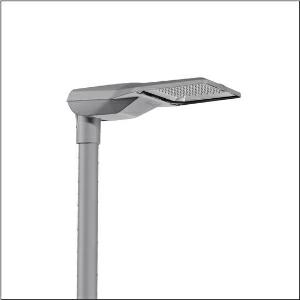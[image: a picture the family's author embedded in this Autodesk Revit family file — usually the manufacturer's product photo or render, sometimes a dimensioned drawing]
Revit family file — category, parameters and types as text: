
# Revit family: streetlight_sl_21_iq_midi___st0_5a_5xe3b41g08mb_6195
name_source: partatom
category: Lighting Fixtures
units: mm (PartAtom-declared; Revit-internal decimal feet)

## family parameters
Cut with Voids When Loaded = No
Host = Face
Light Source = No
Part Type = Normal
Room Calculation Point = No
Round Connector Dimension = Use Diameter
Shared = No

## types (1)
- --- (1 x LED, 20360 lm, 146.7 W, 4000K)
    Apparent Load = 147 VA
    CIE Flux Codes = 41 75 97 100 100
    Color Rendering = 70
    Color Temperature = 4000K
    Default Elevation = 1800 mm
    Description = Streetlight SL 21 iQ midi, mast luminaire, primary light control with lens, of PMMA, primary optical cover: cover, of toughened safety glass, transparent, light distribution: ST0.5a, light emission: direct distribution, primary light characteristic: asymmetric, installation type: post-top, side-entry, LED, High Power LED, rated luminous flux: 20.360lm, luminous efficacy: 139lm/W, light colour: 740, colour temperature: 4000K, control: Street-Remote, Auto-Match, Temp-Guard, Lumen-Switch, Night-Set, Smart-Wire, Light-Fading, Desk-Remote (wireless, voltage-free reading and setting of iQ features in the workshop via application-optimized NFC function/RFID function), optimised constant luminous flux control (CLO 2.0), presetting dimming linear, mains connection: 230..240V, AC, 50/60Hz, start of lifetime: 147W, end of service life: 161W, reduction: 62W, luminaire housing, of diecast aluminium, powder-coated, Siteco® metallic grey (DB 702S), corrosivity category C5 mid according to DIN EN ISO 12944, please order mast flange separately, inclination adjustable: 0°, 5°, 10°, 15°, sealing non-destructively replaceable, multi-level sealing system, length: 644mm, width: 335mm, height: 110mm, mast flange for spigot size: 42mm (side-entry): 5XC10008XM4, 60/48mm (side-entry/post-top): 5XC10108XM2, 76/60mm (side-entry/post-top): 5XC10108XM1, protection rating (complete): IP66, insulation class (complete): insulation class II (safety insulation), certification: CE, ENEC, ENEC+, VDE, impact resistance: IK09, permissible operating ambient temperature for outdoor applications: -40..+50°C, standard-compliant lighting for roads and squares, packaging unit: 1 piece

Light Distribution: ST0.5a
    Height = 111 mm
    Lamp = 1 x LED
    Lamp Light Flux = 20360 lm
    Lamp Power = 146.7 W
    Lamp count = 1
    Length = 644 mm
    Luminous efficacy = 139 lm/W
    Manufacturer = Siteco
    ModVariant = No
    Model = 5XE3B41G08MB
    Number of Poles = 1
    OnlyDefault = Yes
    Power Factor = 1
    Product Name = Streetlight SL 21 iQ midi | ST0.5a
    Product group = mast luminaire | pylon top
    ProductGroupID = 6100
    Protection Class = Protection class II
    Protection Degree = IP 66
    RLX_Detail_Level = 1
    RLX_Emergency_Light_Flux = 0 lm
    RLX_Emergency_Type = 0
    RLX_Emergency_Type_DB = No
    RlxData = <blob elided: 101621 chars, md5=bc9abe9a>
    Socket = socket
    Standby Power = 0 W
    System Light Flux = 20360 lm
    System Power = 147 W
    Type Comments = factory setting: luminous flux: 100 % | dim-lin: 254 | 753 mA
    Type Image = l_1004298.jpg
    URL = http://relux.com
    VarID = @adj_126055
    Voltage = 0 V
    Weight = 0.00 kg
    Width = 336 mm

## geometry (parser evidence)
native form markers: Blend x4, Sweep x11
no freeform markers — native parametric forms only
